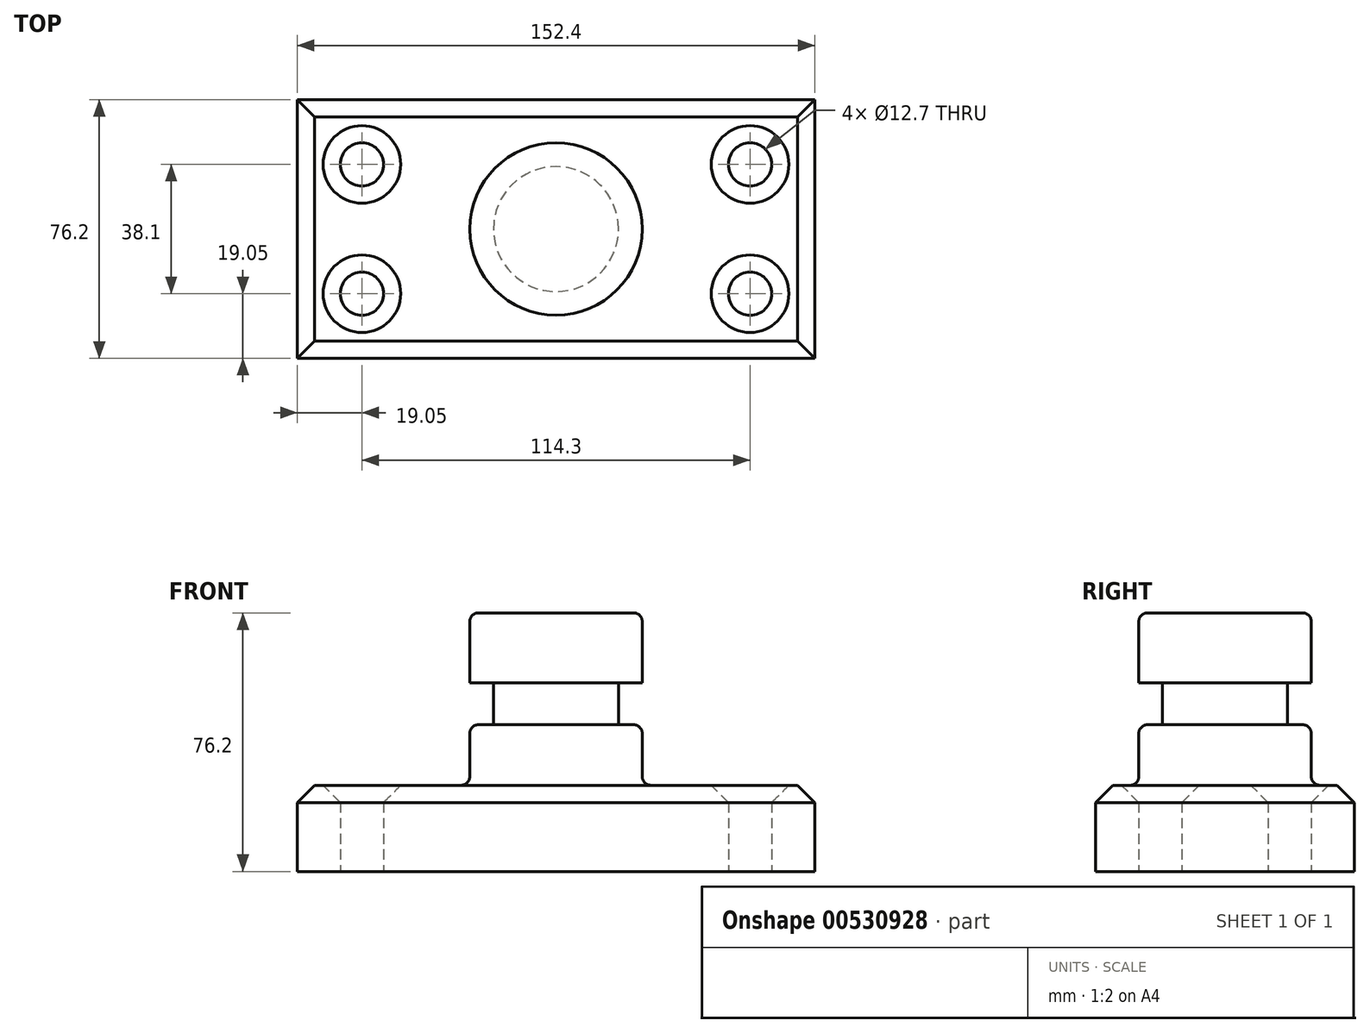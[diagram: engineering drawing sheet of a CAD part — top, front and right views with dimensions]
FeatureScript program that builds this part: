
annotation { "Feature Type Name" : "Feature", "Feature Type Description" : "" }
export const myFeature = defineFeature(function(context is Context, id is Id, definition is map)
    precondition{}
    {
        {
            var Q0;
            Q0=qCreatedBy(makeId("Top.planeOp"),FACE);
            var sketch = newSketch(context, id + "F0", { "sketchPlane" : qUnion([Q0])});
            skLineSegment(sketch, "E0.bottom", {"start": v(-76.2, 38.1) * mm, "end": v(76.2, 38.1) * mm});
            skLineSegment(sketch, "E0.top", {"start": v(-76.2, -38.1) * mm, "end": v(76.2, -38.1) * mm});
            skLineSegment(sketch, "E0.left", {"start": v(-76.2, 38.1) * mm, "end": v(-76.2, -38.1) * mm});
            skLineSegment(sketch, "E0.right", {"start": v(76.2, 38.1) * mm, "end": v(76.2, -38.1) * mm});
            skPoint(sketch, "E0.middle", {"position": v(0, 0) * mm});
            skSolve(sketch);
        }
        {
            var Q0;
            Q0=makeQuery(id+"F0.imprint","IMPRINT",FACE,{"disambiguationData":[TD([[makeQuery(id+"F0.imprint","IMPRINT",EDGE,{"derivedFrom":sQuery(id+"F0.wireOp",EDGE,"E0.bottom")}),-1.0]])]});
            extrude(context, id + "F1", {"entities" : qUnion([Q0]), "depth" : 25.4 * mm, "offsetDistance" : 25.4 * mm});
        }
        {
            var Q0;
            Q0=qCreatedBy(makeId("Top.planeOp"),FACE);
            var sketch = newSketch(context, id + "F2", { "sketchPlane" : qUnion([Q0])});
            skCircle(sketch, "E1", {"center": v(-57.15, 19.05) * mm, "radius": 6.35 * mm});
            skCircle(sketch, "E2", {"center": v(-57.15, -19.05) * mm, "radius": 6.35 * mm});
            skCircle(sketch, "E3", {"center": v(57.15, -19.05) * mm, "radius": 6.35 * mm});
            skCircle(sketch, "E4", {"center": v(57.15, 19.05) * mm, "radius": 6.35 * mm});
            skSolve(sketch);
        }
        {
            var Q0;
            Q0 = qSketchRegion(id + "F2", true);
            extrude(context, id + "F3", {"entities" : qUnion([Q0]), "operationType" : NewBodyOperationType.REMOVE, "endBound" : BoundingType.THROUGH_ALL, "depth" : 25.4 * mm, "offsetDistance" : 25.4 * mm});
        }
        {
            var Q0;
            Q0=makeQuery(id+"F1.opExtrude","CAP_FACE",FACE,{"disambiguationData":[OSD([sQuery(id+"F0.wireOp",EDGE,"E0.bottom"),sQuery(id+"F0.wireOp",EDGE,"E0.top"),sQuery(id+"F0.wireOp",EDGE,"E0.left"),sQuery(id+"F0.wireOp",EDGE,"E0.right")])],"isStart":false});
            chamfer(context, id + "F4", {"entities" : qUnion([Q0]), "width" : 5.08 * mm, "tangentPropagation" : true});
        }
        {
            var Q0;
            Q0=qCreatedBy(makeId("Front.planeOp"),FACE);
            var sketch = newSketch(context, id + "F5", { "sketchPlane" : qUnion([Q0])});
            skLineSegment(sketch, "E5.bottom", {"start": v(0, 25.4) * mm, "end": v(25.4, 25.4) * mm});
            skLineSegment(sketch, "E5.top", {"start": v(0, 76.2) * mm, "end": v(25.4, 76.2) * mm});
            skLineSegment(sketch, "E5.left", {"start": v(0, 25.4) * mm, "end": v(0, 76.2) * mm});
            skLineSegment(sketch, "E5.right", {"start": v(25.4, 25.4) * mm, "end": v(25.4, 76.2) * mm});
            skSolve(sketch);
        }
        {
            var Q0;
            Q0=makeQuery(id+"F5.imprint","IMPRINT",FACE,{"disambiguationData":[TD([[makeQuery(id+"F5.imprint","IMPRINT",EDGE,{"derivedFrom":sQuery(id+"F5.wireOp",EDGE,"E5.bottom")}),1.0]])]});
            var Q1;
            Q1=sQuery(id+"F5.wireOp",EDGE,"E5.left");
            revolve(context, id + "F6", {"operationType" : NewBodyOperationType.ADD, "entities" : qUnion([Q0]), "axis" : qUnion([Q1]), "revolveType" : RevolveType.FULL});
        }
        {
            var Q0;
            Q0=qCreatedBy(makeId("Front.planeOp"),FACE);
            var sketch = newSketch(context, id + "F7", { "sketchPlane" : qUnion([Q0])});
            skLineSegment(sketch, "E6.bottom", {"start": v(28.8, 55.53) * mm, "end": v(18.41, 55.53) * mm});
            skLineSegment(sketch, "E6.top", {"start": v(28.8, 43.24) * mm, "end": v(18.41, 43.24) * mm});
            skLineSegment(sketch, "E6.left", {"start": v(28.8, 55.53) * mm, "end": v(28.8, 43.24) * mm});
            skLineSegment(sketch, "E6.right", {"start": v(18.41, 55.53) * mm, "end": v(18.41, 43.24) * mm});
            skSolve(sketch);
        }
        {
            var Q0;
            Q0=makeQuery(id+"F7.imprint","IMPRINT",FACE,{"disambiguationData":[TD([[makeQuery(id+"F7.imprint","IMPRINT",EDGE,{"derivedFrom":sQuery(id+"F7.wireOp",EDGE,"E6.bottom")}),1.0]])]});
            var Q1;
            Q1=makeQuery(id+"F6.opRevolve","SWEPT_FACE",FACE,{"disambiguationData":[OSD([sQuery(id+"F5.wireOp",EDGE,"E5.right")])]});
            revolve(context, id + "F8", {"operationType" : NewBodyOperationType.REMOVE, "entities" : qUnion([Q0]), "axis" : qUnion([Q1]), "revolveType" : RevolveType.FULL, "oppositeDirection" : true});
        }
        {
            var Q0;
            Q0=makeQuery(id+"F8.boolean.opBoolean","SPLIT",FACE,{"disambiguationData":[TD([makeQuery(id+"F8.opRevolve","SWEPT_FACE",FACE,{"disambiguationData":[OSD([sQuery(id+"F7.wireOp",EDGE,"E6.top")])]})])],"derivedFrom":makeQuery(id+"F6.opRevolve","SWEPT_FACE",FACE,{"disambiguationData":[OSD([sQuery(id+"F5.wireOp",EDGE,"E5.right")])]})});
            fillet(context, id + "F9", {"entities" : qUnion([Q0]), "radius" : 2.54 * mm, "tangentPropagation" : true, "allowEdgeOverflow" : false});
        }
        {
            var Q0;
            Q0=makeQuery(id+"F6.opRevolve","SWEPT_FACE",FACE,{"disambiguationData":[OSD([sQuery(id+"F5.wireOp",EDGE,"E5.top")])]});
            fillet(context, id + "F10", {"entities" : qUnion([Q0]), "radius" : 2.54 * mm, "tangentPropagation" : true, "allowEdgeOverflow" : false});
        }
    });
